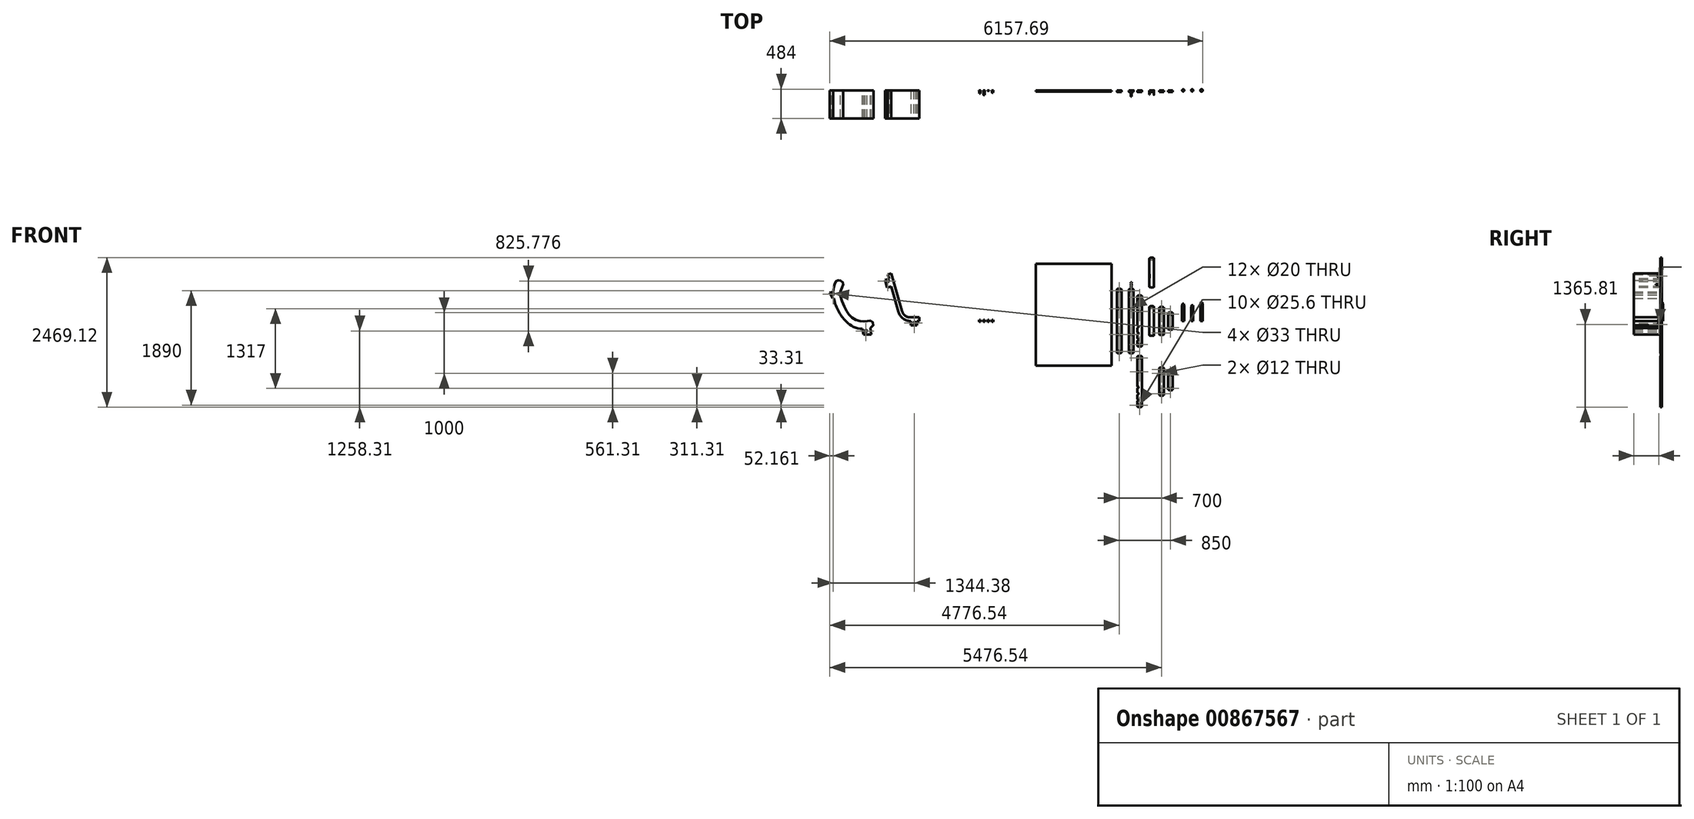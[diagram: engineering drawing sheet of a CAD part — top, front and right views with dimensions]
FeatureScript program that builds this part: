
annotation { "Feature Type Name" : "Feature", "Feature Type Description" : "" }
export const myFeature = defineFeature(function(context is Context, id is Id, definition is map)
    precondition{}
    {
        {
            var Q0;
            Q0=qCreatedBy(makeId("Front.planeOp"),FACE);
            var sketch = newSketch(context, id + "F0", { "sketchPlane" : qUnion([Q0])});
            skLineSegment(sketch, "E0", {"start": v(-38.5, 525.6) * mm, "end": v(-38.5, -525.6) * mm});
            skLineSegment(sketch, "E1", {"start": v(-38.5, -525.6) * mm, "end": v(38.5, -525.6) * mm, "construction": true});
            skLineSegment(sketch, "E2", {"start": v(38.5, -525.6) * mm, "end": v(38.5, 525.6) * mm});
            skLineSegment(sketch, "E3", {"start": v(38.5, 525.6) * mm, "end": v(-38.5, 525.6) * mm, "construction": true});
            skArc(sketch, "E4", {"start": v(38.5, 525.6) * mm, "mid": v(0, 533.3) * mm, "end": v(-38.5, 525.6) * mm});
            skArc(sketch, "E5", {"start": v(-38.5, -525.6) * mm, "mid": v(0, -533.3) * mm, "end": v(38.5, -525.6) * mm});
            skCircle(sketch, "E6", {"center": v(0, 500) * mm, "radius": 12.8 * mm});
            skCircle(sketch, "E7", {"center": v(0, -500) * mm, "radius": 12.8 * mm});
            skPoint(sketch, "E7.centerSnap0", {"position": v(0, 533.3) * mm});
            skCircle(sketch, "E8", {"center": v(0, 205) * mm, "radius": 10 * mm});
            skCircle(sketch, "E9", {"center": v(0, -225) * mm, "radius": 10 * mm});
            skSolve(sketch);
        }
        {
            var Q0;
            Q0=qSketchRegion(id+"F0",true);
            extrude(context, id + "F1", {"entities" : qUnion([Q0]), "depth" : 25 * mm, "offsetDistance" : 25 * mm});
        }
        {
            var Q0;
            Q0=qCreatedBy(makeId("Front.planeOp"),FACE);
            var sketch = newSketch(context, id + "F2", { "sketchPlane" : qUnion([Q0])});
            skCircle(sketch, "E10", {"center": v(138.5, 390) * mm, "radius": 12.8 * mm});
            skCircle(sketch, "E11", {"center": v(138.5, -390) * mm, "radius": 12.8 * mm});
            skLineSegment(sketch, "E12", {"start": v(100, 415.6) * mm, "end": v(100, -415.6) * mm});
            skLineSegment(sketch, "E13", {"start": v(177, 415.6) * mm, "end": v(177, -415.6) * mm});
            skLineSegment(sketch, "E14", {"start": v(138.5, 390) * mm, "end": v(138.5, -390) * mm, "construction": true});
            skLineSegment(sketch, "E15", {"start": v(100, -415.6) * mm, "end": v(177, -415.6) * mm, "construction": true});
            skLineSegment(sketch, "E16", {"start": v(100, 415.6) * mm, "end": v(177, 415.6) * mm, "construction": true});
            skArc(sketch, "E17", {"start": v(177, 415.6) * mm, "mid": v(138.5, 423.3) * mm, "end": v(100, 415.6) * mm});
            skArc(sketch, "E18", {"start": v(100, -415.6) * mm, "mid": v(138.5, -423.3) * mm, "end": v(177, -415.6) * mm});
            skCircle(sketch, "E19", {"center": v(138.5, 160) * mm, "radius": 10 * mm});
            skCircle(sketch, "E20", {"center": v(138.5, -96) * mm, "radius": 12.8 * mm, "construction": true});
            skSolve(sketch);
        }
        {
            var Q0;
            Q0=qSketchRegion(id+"F2",true);
            extrude(context, id + "F3", {"entities" : qUnion([Q0]), "depth" : 25 * mm, "offsetDistance" : 25 * mm});
        }
        {
            var Q0;
            Q0=qCreatedBy(makeId("Front.planeOp"),FACE);
            var sketch = newSketch(context, id + "F4", { "sketchPlane" : qUnion([Q0])});
            skLineSegment(sketch, "E21.bottom", {"start": v(300, 238.1) * mm, "end": v(377, 238.1) * mm, "construction": true});
            skLineSegment(sketch, "E21.top", {"start": v(300, -238.1) * mm, "end": v(377, -238.1) * mm, "construction": true});
            skLineSegment(sketch, "E21.left", {"start": v(300, 238.1) * mm, "end": v(300, -238.1) * mm});
            skLineSegment(sketch, "E21.right", {"start": v(377, 238.1) * mm, "end": v(377, -238.1) * mm});
            skArc(sketch, "E22", {"start": v(377, 238.1) * mm, "mid": v(338.5, 245.8) * mm, "end": v(300, 238.1) * mm});
            skArc(sketch, "E23", {"start": v(300, -238.1) * mm, "mid": v(338.5, -245.8) * mm, "end": v(377, -238.1) * mm});
            skLineSegment(sketch, "E24", {"start": v(317.98, 212.5) * mm, "end": v(377, 212.5) * mm, "construction": true});
            skLineSegment(sketch, "E25", {"start": v(309.25, -212.5) * mm, "end": v(377, -212.5) * mm, "construction": true});
            skSolve(sketch);
        }
        {
            var Q0;
            Q0=qSketchRegion(id+"F4",true);
            extrude(context, id + "F5", {"entities" : qUnion([Q0]), "depth" : 25 * mm, "offsetDistance" : 25 * mm});
        }
        {
            var Q0;
            Q0=makeQuery(id+"F5.opExtrude","SWEPT_FACE",FACE,{"disambiguationData":[OSD([sQuery(id+"F4.wireOp",EDGE,"E21.right")])]});
            var sketch = newSketch(context, id + "F6", { "sketchPlane" : qUnion([Q0])});
            skCircle(sketch, "E26", {"center": v(-12.5, 212.5) * mm, "radius": 6 * mm});
            skSolve(sketch);
        }
        {
            var Q0;
            Q0=qSketchRegion(id+"F6",true);
            var Q1;
            Q1=makeQuery(id+"F5.opExtrude","SWEPT_FACE",FACE,{"disambiguationData":[OSD([sQuery(id+"F4.wireOp",EDGE,"E21.left")])]});
            extrude(context, id + "F7", {"entities" : qUnion([Q0]), "operationType" : NewBodyOperationType.REMOVE, "endBound" : BoundingType.UP_TO_SURFACE, "oppositeDirection" : true, "depth" : 77 * mm, "endBoundEntityFace" : qUnion([Q1]), "offsetDistance" : 25 * mm});
        }
        {
            var Q0;
            Q0=makeQuery(id+"F1.opExtrude","SWEPT_EDGE",EDGE,{"disambiguationData":[OSD([sQuery(id+"F0.wireOp",EDGE,"E2"),sQuery(id+"F0.wireOp",EDGE,"E4")])]});
            var Q1;
            Q1=makeQuery(id+"F1.opExtrude","SWEPT_EDGE",EDGE,{"disambiguationData":[OSD([sQuery(id+"F0.wireOp",EDGE,"E0"),sQuery(id+"F0.wireOp",EDGE,"E4")])]});
            var Q2;
            Q2=makeQuery(id+"F1.opExtrude","SWEPT_EDGE",EDGE,{"disambiguationData":[OSD([sQuery(id+"F0.wireOp",EDGE,"E2"),sQuery(id+"F0.wireOp",EDGE,"E5")])]});
            var Q3;
            Q3=makeQuery(id+"F1.opExtrude","SWEPT_EDGE",EDGE,{"disambiguationData":[OSD([sQuery(id+"F0.wireOp",EDGE,"E0"),sQuery(id+"F0.wireOp",EDGE,"E5")])]});
            var Q4;
            Q4=makeQuery(id+"F3.opExtrude","SWEPT_EDGE",EDGE,{"disambiguationData":[OSD([sQuery(id+"F2.wireOp",EDGE,"E12"),sQuery(id+"F2.wireOp",EDGE,"E18")])]});
            var Q5;
            Q5=makeQuery(id+"F3.opExtrude","SWEPT_EDGE",EDGE,{"disambiguationData":[OSD([sQuery(id+"F2.wireOp",EDGE,"E13"),sQuery(id+"F2.wireOp",EDGE,"E18")])]});
            var Q6;
            Q6=makeQuery(id+"F3.opExtrude","SWEPT_EDGE",EDGE,{"disambiguationData":[OSD([sQuery(id+"F2.wireOp",EDGE,"E12"),sQuery(id+"F2.wireOp",EDGE,"E17")])]});
            var Q7;
            Q7=makeQuery(id+"F3.opExtrude","SWEPT_EDGE",EDGE,{"disambiguationData":[OSD([sQuery(id+"F2.wireOp",EDGE,"E13"),sQuery(id+"F2.wireOp",EDGE,"E17")])]});
            var Q8;
            Q8=makeQuery(id+"F5.opExtrude","SWEPT_EDGE",EDGE,{"disambiguationData":[OSD([sQuery(id+"F4.wireOp",EDGE,"E21.right"),sQuery(id+"F4.wireOp",EDGE,"E23")])]});
            var Q9;
            Q9=makeQuery(id+"F5.opExtrude","SWEPT_EDGE",EDGE,{"disambiguationData":[OSD([sQuery(id+"F4.wireOp",EDGE,"E21.left"),sQuery(id+"F4.wireOp",EDGE,"E23")])]});
            var Q10;
            Q10=makeQuery(id+"F5.opExtrude","SWEPT_EDGE",EDGE,{"disambiguationData":[OSD([sQuery(id+"F4.wireOp",EDGE,"E21.right"),sQuery(id+"F4.wireOp",EDGE,"E22")])]});
            var Q11;
            Q11=makeQuery(id+"F5.opExtrude","SWEPT_EDGE",EDGE,{"disambiguationData":[OSD([sQuery(id+"F4.wireOp",EDGE,"E21.left"),sQuery(id+"F4.wireOp",EDGE,"E22")])]});
            fillet(context, id + "F8", {"entities" : qUnion([Q0, Q1, Q2, Q3, Q4, Q5, Q6, Q7, Q8, Q9, Q10, Q11]), "radius" : 10 * mm, "tangentPropagation" : true, "allowEdgeOverflow" : false});
        }
        {
            var Q0;
            Q0=qCreatedBy(makeId("Front.planeOp"),FACE);
            var sketch = newSketch(context, id + "F9", { "sketchPlane" : qUnion([Q0])});
            skLineSegment(sketch, "E27.bottom", {"start": v(461.5, 225.6) * mm, "end": v(538.5, 225.6) * mm, "construction": true});
            skLineSegment(sketch, "E27.top", {"start": v(461.5, -225.6) * mm, "end": v(538.5, -225.6) * mm, "construction": true});
            skLineSegment(sketch, "E27.left", {"start": v(461.5, 225.6) * mm, "end": v(461.5, -225.6) * mm});
            skLineSegment(sketch, "E27.right", {"start": v(538.5, 225.6) * mm, "end": v(538.5, -225.6) * mm});
            skCircle(sketch, "E28", {"center": v(500, 200) * mm, "radius": 10 * mm});
            skCircle(sketch, "E29", {"center": v(500, -200) * mm, "radius": 12.8 * mm});
            skLineSegment(sketch, "E30", {"start": v(500, 200) * mm, "end": v(500, -200) * mm, "construction": true});
            skArc(sketch, "E31", {"start": v(461.5, -225.6) * mm, "mid": v(500, -233.3) * mm, "end": v(538.5, -225.6) * mm});
            skArc(sketch, "E32", {"start": v(538.5, 225.6) * mm, "mid": v(500, 233.3) * mm, "end": v(461.5, 225.6) * mm});
            skCircle(sketch, "E33", {"center": v(500, 138) * mm, "radius": 6 * mm});
            skSolve(sketch);
        }
        {
            var Q0;
            Q0=qSketchRegion(id+"F9",true);
            extrude(context, id + "F10", {"entities" : qUnion([Q0]), "depth" : 25 * mm, "offsetDistance" : 25 * mm});
        }
        {
            var Q0;
            Q0=qCreatedBy(makeId("Front.planeOp"),FACE);
            var sketch = newSketch(context, id + "F11", { "sketchPlane" : qUnion([Q0])});
            skLineSegment(sketch, "E34.bottom", {"start": v(611.5, 135.6) * mm, "end": v(688.5, 135.6) * mm, "construction": true});
            skLineSegment(sketch, "E34.top", {"start": v(611.5, -137.6) * mm, "end": v(688.5, -137.6) * mm, "construction": true});
            skLineSegment(sketch, "E34.left", {"start": v(611.5, 135.6) * mm, "end": v(611.5, -137.6) * mm});
            skLineSegment(sketch, "E34.right", {"start": v(688.5, 135.6) * mm, "end": v(688.5, -137.6) * mm});
            skCircle(sketch, "E35", {"center": v(650, 110) * mm, "radius": 10 * mm});
            skCircle(sketch, "E36", {"center": v(650, -112) * mm, "radius": 10 * mm});
            skLineSegment(sketch, "E37", {"start": v(650, 110) * mm, "end": v(650, -112) * mm, "construction": true});
            skArc(sketch, "E38", {"start": v(688.5, 135.6) * mm, "mid": v(650, 143.3) * mm, "end": v(611.5, 135.6) * mm});
            skArc(sketch, "E39", {"start": v(611.5, -137.6) * mm, "mid": v(650, -145.3) * mm, "end": v(688.5, -137.6) * mm});
            skLineSegment(sketch, "E40", {"start": v(591.68, 162.5) * mm, "end": v(739.94, 162.5) * mm, "construction": true});
            skSolve(sketch);
        }
        {
            var Q0;
            Q0=qSketchRegion(id+"F11",true);
            extrude(context, id + "F12", {"entities" : qUnion([Q0]), "depth" : 25 * mm, "offsetDistance" : 25 * mm});
        }
        {
            var Q0;
            Q0=qCreatedBy(makeId("Front.planeOp"),FACE);
            var sketch = newSketch(context, id + "F13", { "sketchPlane" : qUnion([Q0])});
            skLineSegment(sketch, "E41.bottom", {"start": v(-1573.72, 942.98) * mm, "end": v(-325.98, 942.98) * mm});
            skLineSegment(sketch, "E41.top", {"start": v(-1573.72, -735.53) * mm, "end": v(-325.98, -735.53) * mm});
            skLineSegment(sketch, "E41.left", {"start": v(-1573.72, 942.98) * mm, "end": v(-1573.72, -735.53) * mm});
            skLineSegment(sketch, "E41.right", {"start": v(-325.98, 942.98) * mm, "end": v(-325.98, -735.53) * mm});
            skSolve(sketch);
        }
        {
            var Q0;
            Q0=qSketchRegion(id+"F13",true);
            extrude(context, id + "F14", {"entities" : qUnion([Q0]), "depth" : 20 * mm, "offsetDistance" : 25 * mm});
        }
        {
            var Q0;
            Q0=qCreatedBy(makeId("Top.planeOp"),FACE);
            var sketch = newSketch(context, id + "F15", { "sketchPlane" : qUnion([Q0])});
            skCircle(sketch, "E42", {"center": v(857.86, 0) * mm, "radius": 17.5 * mm});
            skSolve(sketch);
        }
        {
            var Q0;
            Q0=qSketchRegion(id+"F15",true);
            extrude(context, id + "F16", {"entities" : qUnion([Q0]), "depth" : 257 * mm, "offsetDistance" : 25 * mm, "hasSecondDirection" : true, "secondDirectionOppositeDirection" : true, "secondDirectionDepth" : 257 * mm});
        }
        {
            var Q0;
            Q0=qCreatedBy(makeId("Top.planeOp"),FACE);
            var sketch = newSketch(context, id + "F17", { "sketchPlane" : qUnion([Q0])});
            skCircle(sketch, "E43", {"center": v(1007, 0) * mm, "radius": 17.5 * mm});
            skSolve(sketch);
        }
        {
            var Q0;
            Q0=qSketchRegion(id+"F17",true);
            extrude(context, id + "F18", {"entities" : qUnion([Q0]), "depth" : 232 * mm, "offsetDistance" : 25 * mm, "hasSecondDirection" : true, "secondDirectionOppositeDirection" : true, "secondDirectionDepth" : 232 * mm});
        }
        {
            var Q0;
            Q0=qCreatedBy(makeId("Top.planeOp"),FACE);
            var sketch = newSketch(context, id + "F19", { "sketchPlane" : qUnion([Q0])});
            skCircle(sketch, "E44", {"center": v(1161.15, 0) * mm, "radius": 20 * mm});
            skSolve(sketch);
        }
        {
            var Q0;
            Q0=qSketchRegion(id+"F19",true);
            extrude(context, id + "F20", {"entities" : qUnion([Q0]), "depth" : 282 * mm, "offsetDistance" : 25 * mm, "hasSecondDirection" : true, "secondDirectionOppositeDirection" : true, "secondDirectionDepth" : 282 * mm});
        }
        {
            var Q0;
            Q0=makeQuery(id+"F3.opExtrude","CAP_FACE",FACE,{"disambiguationData":[OSD([sQuery(id+"F2.wireOp",EDGE,"E10"),sQuery(id+"F2.wireOp",EDGE,"E11"),sQuery(id+"F2.wireOp",EDGE,"E12"),sQuery(id+"F2.wireOp",EDGE,"E13"),sQuery(id+"F2.wireOp",EDGE,"E17"),sQuery(id+"F2.wireOp",EDGE,"E18"),sQuery(id+"F2.wireOp",EDGE,"E19")])],"isStart":false});
            var sketch = newSketch(context, id + "F21", { "sketchPlane" : qUnion([Q0])});
            skCircle(sketch, "E45", {"center": v(100, -96) * mm, "radius": 20 * mm});
            skLineSegment(sketch, "E46", {"start": v(138.5, 160) * mm, "end": v(59.14, 160) * mm, "construction": true});
            skSolve(sketch);
        }
        {
            var Q0;
            Q0=qSketchRegion(id+"F21",true);
            extrude(context, id + "F22", {"entities" : qUnion([Q0]), "operationType" : NewBodyOperationType.REMOVE, "oppositeDirection" : true, "depth" : 25 * mm, "offsetDistance" : 25 * mm});
        }
        {
            var Q0;
            Q0=makeQuery(id+"F5.opExtrude","SWEPT_FACE",FACE,{"disambiguationData":[OSD([sQuery(id+"F4.wireOp",EDGE,"E21.right")])]});
            var sketch = newSketch(context, id + "F23", { "sketchPlane" : qUnion([Q0])});
            skLineSegment(sketch, "E47", {"start": v(-28, -27.5) * mm, "end": v(-28, -87.5) * mm});
            skLineSegment(sketch, "E48", {"start": v(-28, -87.5) * mm, "end": v(-59.23, -76.33) * mm});
            skLineSegment(sketch, "E49", {"start": v(-28, -27.5) * mm, "end": v(-59.23, -38.67) * mm});
            skArc(sketch, "E50", {"start": v(-59.23, -38.67) * mm, "mid": v(-72.5, -57.5) * mm, "end": v(-59.23, -76.33) * mm});
            skCircle(sketch, "E51", {"center": v(-52.5, -57.5) * mm, "radius": 10 * mm});
            skLineSegment(sketch, "E52", {"start": v(-52.5, -57.5) * mm, "end": v(29.16, -57.5) * mm, "construction": true});
            skCircle(sketch, "E53.0", {"center": v(-12.5, 212.5) * mm, "radius": 6 * mm, "construction": true});
            skSolve(sketch);
        }
        {
            var Q0;
            Q0=makeQuery(id+"F5.opExtrude","CAP_FACE",FACE,{"disambiguationData":[OSD([sQuery(id+"F4.wireOp",EDGE,"E21.left"),sQuery(id+"F4.wireOp",EDGE,"E21.right"),sQuery(id+"F4.wireOp",EDGE,"E22"),sQuery(id+"F4.wireOp",EDGE,"E23")])],"isStart":false});
            var sketch = newSketch(context, id + "F24", { "sketchPlane" : qUnion([Q0])});
            skLineSegment(sketch, "E54.bottom", {"start": v(372, -27.5) * mm, "end": v(377, -27.5) * mm});
            skLineSegment(sketch, "E54.top", {"start": v(372, -87.5) * mm, "end": v(377, -87.5) * mm});
            skLineSegment(sketch, "E54.left", {"start": v(372, -27.5) * mm, "end": v(372, -87.5) * mm});
            skLineSegment(sketch, "E54.right", {"start": v(377, -27.5) * mm, "end": v(377, -87.5) * mm});
            skSolve(sketch);
        }
        {
            var Q0;
            Q0=makeQuery(id+"F5.opExtrude","SWEPT_BODY",BODY,{"disambiguationData":[OSD([sQuery(id+"F4.wireOp",EDGE,"E21.left"),sQuery(id+"F4.wireOp",EDGE,"E21.right"),sQuery(id+"F4.wireOp",EDGE,"E22"),sQuery(id+"F4.wireOp",EDGE,"E23")])]});
            transform(context, id + "F25", {"entities" : qUnion([Q0]), "transformType" : TransformType.TRANSLATION_3D, "dx" : 0 * mm, "dy" : 0 * mm, "dz" : 800 * mm, "makeCopy" : true});
        }
        {
            var Q0;
            Q0=makeQuery(id+"F24.imprint","IMPRINT",FACE,{"disambiguationData":[TD([[makeQuery(id+"F24.imprint","IMPRINT",EDGE,{"derivedFrom":sQuery(id+"F24.wireOp",EDGE,"E54.bottom")}),-1.0]])]});
            extrude(context, id + "F26", {"entities" : qUnion([Q0]), "operationType" : NewBodyOperationType.ADD, "depth" : 3 * mm, "offsetDistance" : 25 * mm});
        }
        {
            var Q0;
            Q0=makeQuery(id+"F3.opExtrude","CAP_FACE",FACE,{"disambiguationData":[OSD([sQuery(id+"F2.wireOp",EDGE,"E10"),sQuery(id+"F2.wireOp",EDGE,"E11"),sQuery(id+"F2.wireOp",EDGE,"E12"),sQuery(id+"F2.wireOp",EDGE,"E13"),sQuery(id+"F2.wireOp",EDGE,"E17"),sQuery(id+"F2.wireOp",EDGE,"E18"),sQuery(id+"F2.wireOp",EDGE,"E19")])],"isStart":false});
            var sketch = newSketch(context, id + "F27", { "sketchPlane" : qUnion([Q0])});
            skCircle(sketch, "E55", {"center": v(100, -306) * mm, "radius": 20 * mm});
            skArc(sketch, "E56.0", {"start": v(100, -116) * mm, "mid": v(120, -96) * mm, "end": v(100, -76) * mm, "construction": true});
            skCircle(sketch, "E57", {"center": v(100, -201) * mm, "radius": 20 * mm});
            skSolve(sketch);
        }
        {
            var Q0;
            Q0=qSketchRegion(id+"F27",true);
            extrude(context, id + "F28", {"entities" : qUnion([Q0]), "operationType" : NewBodyOperationType.REMOVE, "oppositeDirection" : true, "depth" : 25 * mm, "offsetDistance" : 25 * mm});
        }
        {
            var Q0;
            Q0=qSketchRegion(id+"F23",true);
            extrude(context, id + "F29", {"entities" : qUnion([Q0]), "operationType" : NewBodyOperationType.ADD, "oppositeDirection" : true, "depth" : 5 * mm, "offsetDistance" : 25 * mm});
        }
        {
            var Q0;
            Q0=makeQuery(id+"F22.boolean.opBoolean","COPY",FACE,{"derivedFrom":makeQuery(id+"F22.opExtrude","SWEPT_FACE",FACE,{"disambiguationData":[OSD([sQuery(id+"F21.wireOp",EDGE,"E45")])]})});
            var Q1;
            Q1=makeQuery(id+"F28.boolean.opBoolean","COPY",FACE,{"derivedFrom":makeQuery(id+"F28.opExtrude","SWEPT_FACE",FACE,{"disambiguationData":[OSD([sQuery(id+"F27.wireOp",EDGE,"E57")])]})});
            var Q2;
            Q2=makeQuery(id+"F28.boolean.opBoolean","COPY",FACE,{"derivedFrom":makeQuery(id+"F28.opExtrude","SWEPT_FACE",FACE,{"disambiguationData":[OSD([sQuery(id+"F27.wireOp",EDGE,"E55")])]})});
            fillet(context, id + "F30", {"entities" : qUnion([Q0, Q1, Q2]), "radius" : 2 * mm, "tangentPropagation" : true, "allowEdgeOverflow" : false});
        }
        {
            var Q0;
            Q0=qCreatedBy(makeId("Front.planeOp"),FACE);
            var sketch = newSketch(context, id + "F31", { "sketchPlane" : qUnion([Q0])});
            skLineSegment(sketch, "E58", {"start": v(-3800, 0) * mm, "end": v(-3500, 0) * mm});
            skLineSegment(sketch, "E59", {"start": v(-3500, 0) * mm, "end": v(-3500, 60) * mm});
            skLineSegment(sketch, "E60", {"start": v(-3500, 60) * mm, "end": v(-3754.65, 60) * mm});
            skLineSegment(sketch, "E61", {"start": v(-3754.65, 60) * mm, "end": v(-3960.53, 786.02) * mm});
            skLineSegment(sketch, "E62", {"start": v(-3960.53, 786.02) * mm, "end": v(-4018.26, 769.65) * mm});
            skLineSegment(sketch, "E63", {"start": v(-4018.26, 769.65) * mm, "end": v(-3800, 0) * mm});
            skSolve(sketch);
        }
        {
            var Q0;
            Q0=qSketchRegion(id+"F31",true);
            extrude(context, id + "F32", {"entities" : qUnion([Q0]), "depth" : 464 * mm, "offsetDistance" : 25 * mm});
        }
        {
            var Q0;
            Q0=makeQuery(id+"F1.opExtrude","SWEPT_BODY",BODY,{"disambiguationData":[OSD([sQuery(id+"F0.wireOp",EDGE,"E0"),sQuery(id+"F0.wireOp",EDGE,"E2"),sQuery(id+"F0.wireOp",EDGE,"E4"),sQuery(id+"F0.wireOp",EDGE,"E5"),sQuery(id+"F0.wireOp",EDGE,"E6"),sQuery(id+"F0.wireOp",EDGE,"E7"),sQuery(id+"F0.wireOp",EDGE,"E8"),sQuery(id+"F0.wireOp",EDGE,"E9")])]});
            transform(context, id + "F33", {"entities" : qUnion([Q0]), "transformType" : TransformType.TRANSLATION_3D, "dx" : -200 * mm, "dy" : 0 * mm, "dz" : 0 * mm, "makeCopy" : true});
        }
        {
            var Q0;
            Q0=makeQuery(id+"F3.opExtrude","SWEPT_BODY",BODY,{"disambiguationData":[OSD([sQuery(id+"F2.wireOp",EDGE,"E10"),sQuery(id+"F2.wireOp",EDGE,"E11"),sQuery(id+"F2.wireOp",EDGE,"E12"),sQuery(id+"F2.wireOp",EDGE,"E13"),sQuery(id+"F2.wireOp",EDGE,"E17"),sQuery(id+"F2.wireOp",EDGE,"E18"),sQuery(id+"F2.wireOp",EDGE,"E19")])]});
            transform(context, id + "F34", {"entities" : qUnion([Q0]), "transformType" : TransformType.TRANSLATION_3D, "dx" : 0 * mm, "dy" : 0 * mm, "dz" : -1000 * mm, "makeCopy" : true});
        }
        {
            var Q0;
            Q0=makeQuery(id+"F10.opExtrude","SWEPT_BODY",BODY,{"disambiguationData":[OSD([sQuery(id+"F9.wireOp",EDGE,"E27.left"),sQuery(id+"F9.wireOp",EDGE,"E27.right"),sQuery(id+"F9.wireOp",EDGE,"E28"),sQuery(id+"F9.wireOp",EDGE,"E29"),sQuery(id+"F9.wireOp",EDGE,"E31"),sQuery(id+"F9.wireOp",EDGE,"E32"),sQuery(id+"F9.wireOp",EDGE,"E33")])]});
            transform(context, id + "F35", {"entities" : qUnion([Q0]), "transformType" : TransformType.TRANSLATION_3D, "dx" : 0 * mm, "dy" : 0 * mm, "dz" : -1000 * mm, "makeCopy" : true});
        }
        {
            var Q0;
            Q0=makeQuery(id+"F12.opExtrude","SWEPT_BODY",BODY,{"disambiguationData":[OSD([sQuery(id+"F11.wireOp",EDGE,"E34.left"),sQuery(id+"F11.wireOp",EDGE,"E34.right"),sQuery(id+"F11.wireOp",EDGE,"E35"),sQuery(id+"F11.wireOp",EDGE,"E36"),sQuery(id+"F11.wireOp",EDGE,"E38"),sQuery(id+"F11.wireOp",EDGE,"E39")])]});
            transform(context, id + "F36", {"entities" : qUnion([Q0]), "transformType" : TransformType.TRANSLATION_3D, "dx" : 0 * mm, "dy" : 0 * mm, "dz" : -1000 * mm, "makeCopy" : true});
        }
        {
            var Q0;
            Q0=makeQuery(id+"F32.opExtrude","SWEPT_EDGE",EDGE,{"disambiguationData":[OSD([sQuery(id+"F31.wireOp",EDGE,"E58"),sQuery(id+"F31.wireOp",EDGE,"E63")])]});
            fillet(context, id + "F37", {"entities" : qUnion([Q0]), "radius" : 200 * mm, "tangentPropagation" : true, "allowEdgeOverflow" : false});
        }
        {
            var Q0;
            Q0=makeQuery(id+"F32.opExtrude","SWEPT_EDGE",EDGE,{"disambiguationData":[OSD([sQuery(id+"F31.wireOp",EDGE,"E60"),sQuery(id+"F31.wireOp",EDGE,"E61")])]});
            fillet(context, id + "F38", {"entities" : qUnion([Q0]), "radius" : 140 * mm, "tangentPropagation" : true, "allowEdgeOverflow" : false});
        }
        {
            var Q0;
            Q0=makeQuery(id+"F32.opExtrude","CAP_FACE",FACE,{"disambiguationData":[OSD([sQuery(id+"F31.wireOp",EDGE,"E58"),sQuery(id+"F31.wireOp",EDGE,"E59"),sQuery(id+"F31.wireOp",EDGE,"E60"),sQuery(id+"F31.wireOp",EDGE,"E61"),sQuery(id+"F31.wireOp",EDGE,"E62"),sQuery(id+"F31.wireOp",EDGE,"E63")])],"isStart":false});
            var sketch = newSketch(context, id + "F39", { "sketchPlane" : qUnion([Q0])});
            skPoint(sketch, "E64", {"position": v(-4018.56, 660.78) * mm});
            skPoint(sketch, "E65", {"position": v(-3580, -30) * mm});
            skLineSegment(sketch, "E66", {"start": v(-4018.56, 660.78) * mm, "end": v(-3931.98, 685.33) * mm, "construction": true});
            skLineSegment(sketch, "E67", {"start": v(-3580, -30) * mm, "end": v(-3580, 60) * mm, "construction": true});
            skCircle(sketch, "E68", {"center": v(-4018.56, 660.78) * mm, "radius": 16.5 * mm});
            skCircle(sketch, "E69", {"center": v(-3580, -30) * mm, "radius": 16.5 * mm});
            skLineSegment(sketch, "E70", {"start": v(-3997.89, 697.82) * mm, "end": v(-4065.23, 678.73) * mm});
            skLineSegment(sketch, "E71", {"start": v(-4065.23, 678.73) * mm, "end": v(-4029.77, 553.66) * mm});
            skLineSegment(sketch, "E72", {"start": v(-4029.77, 553.66) * mm, "end": v(-3962.42, 572.75) * mm});
            skLineSegment(sketch, "E73.bottom", {"start": v(-3540, 0) * mm, "end": v(-3640, 0) * mm});
            skLineSegment(sketch, "E73.top", {"start": v(-3540, -70) * mm, "end": v(-3640, -70) * mm});
            skLineSegment(sketch, "E73.left", {"start": v(-3540, 0) * mm, "end": v(-3540, -70) * mm});
            skLineSegment(sketch, "E73.right", {"start": v(-3640, 0) * mm, "end": v(-3640, -70) * mm});
            skSolve(sketch);
        }
        {
            var Q0;
            Q0=makeQuery(id+"F39.imprint","IMPRINT",FACE,{"disambiguationData":[TD([[makeQuery(id+"F39.imprint","IMPRINT",EDGE,{"derivedFrom":sQuery(id+"F39.wireOp",EDGE,"E69")}),-1.0]])]});
            var Q1;
            Q1=makeQuery(id+"F39.imprint","IMPRINT",FACE,{"disambiguationData":[TD([[makeQuery(id+"F39.imprint","IMPRINT",EDGE,{"derivedFrom":sQuery(id+"F39.wireOp",EDGE,"E68")}),-1.0]])]});
            var Q2;
            Q2=makeQuery(id+"F32.opExtrude","CAP_FACE",FACE,{"disambiguationData":[OSD([sQuery(id+"F31.wireOp",EDGE,"E58"),sQuery(id+"F31.wireOp",EDGE,"E59"),sQuery(id+"F31.wireOp",EDGE,"E60"),sQuery(id+"F31.wireOp",EDGE,"E61"),sQuery(id+"F31.wireOp",EDGE,"E62"),sQuery(id+"F31.wireOp",EDGE,"E63")])],"isStart":true});
            extrude(context, id + "F40", {"entities" : qUnion([Q0, Q1]), "operationType" : NewBodyOperationType.ADD, "endBound" : BoundingType.UP_TO_SURFACE, "oppositeDirection" : true, "depth" : 25 * mm, "endBoundEntityFace" : qUnion([Q2]), "offsetDistance" : 25 * mm});
        }
        {
            var Q0;
            Q0=makeQuery(id+"F16.opExtrude","CAP_FACE",FACE,{"disambiguationData":[OSD([sQuery(id+"F15.wireOp",EDGE,"E42")])],"isStart":false});
            var sketch = newSketch(context, id + "F41", { "sketchPlane" : qUnion([Q0])});
            skCircle(sketch, "E74", {"center": v(857.86, 0) * mm, "radius": 12.8 * mm});
            skSolve(sketch);
        }
        {
            var Q0;
            Q0=qSketchRegion(id+"F41",true);
            extrude(context, id + "F42", {"entities" : qUnion([Q0]), "operationType" : NewBodyOperationType.ADD, "depth" : 25 * mm, "offsetDistance" : 25 * mm});
        }
        {
            var Q0;
            Q0=makeQuery(id+"F16.opExtrude","CAP_FACE",FACE,{"disambiguationData":[OSD([sQuery(id+"F15.wireOp",EDGE,"E42")])],"isStart":true});
            var sketch = newSketch(context, id + "F43", { "sketchPlane" : qUnion([Q0])});
            skCircle(sketch, "E75", {"center": v(857.86, 0) * mm, "radius": 12.8 * mm});
            skSolve(sketch);
        }
        {
            var Q0;
            Q0=qSketchRegion(id+"F43",true);
            extrude(context, id + "F44", {"entities" : qUnion([Q0]), "operationType" : NewBodyOperationType.ADD, "depth" : 25 * mm, "offsetDistance" : 25 * mm});
        }
        {
            var Q0;
            Q0=makeQuery(id+"F18.opExtrude","CAP_FACE",FACE,{"disambiguationData":[OSD([sQuery(id+"F17.wireOp",EDGE,"E43")])],"isStart":true});
            var sketch = newSketch(context, id + "F45", { "sketchPlane" : qUnion([Q0])});
            skCircle(sketch, "E76", {"center": v(1007, 0) * mm, "radius": 12.8 * mm});
            skSolve(sketch);
        }
        {
            var Q0;
            Q0=qSketchRegion(id+"F45",true);
            extrude(context, id + "F46", {"entities" : qUnion([Q0]), "operationType" : NewBodyOperationType.ADD, "depth" : 25 * mm, "offsetDistance" : 25 * mm});
        }
        {
            var Q0;
            Q0=makeQuery(id+"F18.opExtrude","CAP_FACE",FACE,{"disambiguationData":[OSD([sQuery(id+"F17.wireOp",EDGE,"E43")])],"isStart":false});
            var sketch = newSketch(context, id + "F47", { "sketchPlane" : qUnion([Q0])});
            skCircle(sketch, "E77", {"center": v(1007, 0) * mm, "radius": 12.8 * mm});
            skSolve(sketch);
        }
        {
            var Q0;
            Q0=qSketchRegion(id+"F47",true);
            extrude(context, id + "F48", {"entities" : qUnion([Q0]), "operationType" : NewBodyOperationType.ADD, "depth" : 25 * mm, "offsetDistance" : 25 * mm});
        }
        {
            var Q0;
            Q0=makeQuery(id+"F20.opExtrude","CAP_FACE",FACE,{"disambiguationData":[OSD([sQuery(id+"F19.wireOp",EDGE,"E44")])],"isStart":true});
            var sketch = newSketch(context, id + "F49", { "sketchPlane" : qUnion([Q0])});
            skCircle(sketch, "E78", {"center": v(1161.15, 0) * mm, "radius": 12.8 * mm});
            skSolve(sketch);
        }
        {
            var Q0;
            Q0=qSketchRegion(id+"F49",true);
            extrude(context, id + "F50", {"entities" : qUnion([Q0]), "operationType" : NewBodyOperationType.ADD, "depth" : 25 * mm, "offsetDistance" : 25 * mm});
        }
        {
            var Q0;
            Q0=makeQuery(id+"F20.opExtrude","CAP_FACE",FACE,{"disambiguationData":[OSD([sQuery(id+"F19.wireOp",EDGE,"E44")])],"isStart":false});
            var sketch = newSketch(context, id + "F51", { "sketchPlane" : qUnion([Q0])});
            skCircle(sketch, "E79", {"center": v(1161.15, 0) * mm, "radius": 12.8 * mm});
            skSolve(sketch);
        }
        {
            var Q0;
            Q0=qSketchRegion(id+"F51",true);
            extrude(context, id + "F52", {"entities" : qUnion([Q0]), "operationType" : NewBodyOperationType.ADD, "depth" : 25 * mm, "offsetDistance" : 25 * mm});
        }
        {
            var Q0;
            Q0=qCreatedBy(makeId("Front.planeOp"),FACE);
            var sketch = newSketch(context, id + "F53", { "sketchPlane" : qUnion([Q0])});
            skCircle(sketch, "E80", {"center": v(-2500, 0) * mm, "radius": 15 * mm, "construction": true});
            skLineSegment(sketch, "E81.0", {"start": v(-2508.66, 15) * mm, "end": v(-2491.34, 15) * mm});
            skLineSegment(sketch, "E81.1", {"start": v(-2491.34, 15) * mm, "end": v(-2482.68, 0) * mm});
            skLineSegment(sketch, "E81.2", {"start": v(-2482.68, 0) * mm, "end": v(-2491.34, -15) * mm});
            skLineSegment(sketch, "E81.3", {"start": v(-2491.34, -15) * mm, "end": v(-2508.66, -15) * mm});
            skLineSegment(sketch, "E81.4", {"start": v(-2508.66, -15) * mm, "end": v(-2517.32, 0) * mm});
            skLineSegment(sketch, "E81.5", {"start": v(-2517.32, 0) * mm, "end": v(-2508.66, 15) * mm});
            skPoint(sketch, "E81.0.midPoint", {"position": v(-2500, 15) * mm});
            skCircle(sketch, "E82", {"center": v(-2500, 0) * mm, "radius": 21 * mm, "construction": true});
            skCircle(sketch, "E83.cCircle", {"center": v(-2430, 0) * mm, "radius": 15 * mm, "construction": true});
            skLineSegment(sketch, "E83.0", {"start": v(-2438.66, 15) * mm, "end": v(-2421.34, 15) * mm});
            skLineSegment(sketch, "E83.1", {"start": v(-2421.34, 15) * mm, "end": v(-2412.68, 0) * mm});
            skLineSegment(sketch, "E83.2", {"start": v(-2412.68, 0) * mm, "end": v(-2421.34, -15) * mm});
            skLineSegment(sketch, "E83.3", {"start": v(-2421.34, -15) * mm, "end": v(-2438.66, -15) * mm});
            skLineSegment(sketch, "E83.4", {"start": v(-2438.66, -15) * mm, "end": v(-2447.32, 0) * mm});
            skLineSegment(sketch, "E83.5", {"start": v(-2447.32, 0) * mm, "end": v(-2438.66, 15) * mm});
            skPoint(sketch, "E83.0.midPoint", {"position": v(-2430, 15) * mm});
            skCircle(sketch, "E84.cCircle", {"center": v(-2360, 0) * mm, "radius": 15 * mm, "construction": true});
            skLineSegment(sketch, "E84.0", {"start": v(-2368.66, 15) * mm, "end": v(-2351.34, 15) * mm});
            skLineSegment(sketch, "E84.1", {"start": v(-2351.34, 15) * mm, "end": v(-2342.68, 0) * mm});
            skLineSegment(sketch, "E84.2", {"start": v(-2342.68, 0) * mm, "end": v(-2351.34, -15) * mm});
            skLineSegment(sketch, "E84.3", {"start": v(-2351.34, -15) * mm, "end": v(-2368.66, -15) * mm});
            skLineSegment(sketch, "E84.4", {"start": v(-2368.66, -15) * mm, "end": v(-2377.32, 0) * mm});
            skLineSegment(sketch, "E84.5", {"start": v(-2377.32, 0) * mm, "end": v(-2368.66, 15) * mm});
            skPoint(sketch, "E84.0.midPoint", {"position": v(-2360, 15) * mm});
            skCircle(sketch, "E85", {"center": v(-2360, 0) * mm, "radius": 10 * mm});
            skCircle(sketch, "E86.cCircle", {"center": v(-2290, 0) * mm, "radius": 15 * mm, "construction": true});
            skLineSegment(sketch, "E86.0", {"start": v(-2298.66, 15) * mm, "end": v(-2281.34, 15) * mm});
            skLineSegment(sketch, "E86.1", {"start": v(-2281.34, 15) * mm, "end": v(-2272.68, 0) * mm});
            skLineSegment(sketch, "E86.2", {"start": v(-2272.68, 0) * mm, "end": v(-2281.34, -15) * mm});
            skLineSegment(sketch, "E86.3", {"start": v(-2281.34, -15) * mm, "end": v(-2298.66, -15) * mm});
            skLineSegment(sketch, "E86.4", {"start": v(-2298.66, -15) * mm, "end": v(-2307.32, 0) * mm});
            skLineSegment(sketch, "E86.5", {"start": v(-2307.32, 0) * mm, "end": v(-2298.66, 15) * mm});
            skPoint(sketch, "E86.0.midPoint", {"position": v(-2290, 15) * mm});
            skSolve(sketch);
        }
        {
            var Q0;
            Q0=qSketchRegion(id+"F53",true);
            extrude(context, id + "F54", {"entities" : qUnion([Q0]), "depth" : 8 * mm, "offsetDistance" : 25 * mm});
        }
        {
            var Q0;
            Q0=makeQuery(id+"F54.opExtrude","CAP_FACE",FACE,{"disambiguationData":[OSD([sQuery(id+"F53.wireOp",EDGE,"E81.0"),sQuery(id+"F53.wireOp",EDGE,"E81.1"),sQuery(id+"F53.wireOp",EDGE,"E81.2"),sQuery(id+"F53.wireOp",EDGE,"E81.3"),sQuery(id+"F53.wireOp",EDGE,"E81.4"),sQuery(id+"F53.wireOp",EDGE,"E81.5")])],"isStart":false});
            var sketch = newSketch(context, id + "F55", { "sketchPlane" : qUnion([Q0])});
            skCircle(sketch, "E87", {"center": v(-2500, 0) * mm, "radius": 10 * mm});
            skPoint(sketch, "E87.centerSnap0", {"position": v(-2500, 15) * mm});
            skSolve(sketch);
        }
        {
            var Q0;
            Q0=qSketchRegion(id+"F55",true);
            extrude(context, id + "F56", {"entities" : qUnion([Q0]), "operationType" : NewBodyOperationType.ADD, "depth" : 42 * mm, "offsetDistance" : 25 * mm});
        }
        {
            var Q0;
            Q0=makeQuery(id+"F54.opExtrude","CAP_FACE",FACE,{"disambiguationData":[OSD([sQuery(id+"F53.wireOp",EDGE,"E83.0"),sQuery(id+"F53.wireOp",EDGE,"E83.1"),sQuery(id+"F53.wireOp",EDGE,"E83.2"),sQuery(id+"F53.wireOp",EDGE,"E83.3"),sQuery(id+"F53.wireOp",EDGE,"E83.4"),sQuery(id+"F53.wireOp",EDGE,"E83.5")])],"isStart":false});
            var sketch = newSketch(context, id + "F57", { "sketchPlane" : qUnion([Q0])});
            skCircle(sketch, "E88", {"center": v(-2430, 0) * mm, "radius": 10 * mm});
            skSolve(sketch);
        }
        {
            var Q0;
            Q0=qSketchRegion(id+"F57",true);
            extrude(context, id + "F58", {"entities" : qUnion([Q0]), "operationType" : NewBodyOperationType.ADD, "depth" : 67 * mm, "offsetDistance" : 25 * mm});
        }
        {
            var Q0;
            Q0=makeQuery(id+"F54.opExtrude","CAP_FACE",FACE,{"disambiguationData":[OSD([sQuery(id+"F53.wireOp",EDGE,"E86.0"),sQuery(id+"F53.wireOp",EDGE,"E86.1"),sQuery(id+"F53.wireOp",EDGE,"E86.2"),sQuery(id+"F53.wireOp",EDGE,"E86.3"),sQuery(id+"F53.wireOp",EDGE,"E86.4"),sQuery(id+"F53.wireOp",EDGE,"E86.5")])],"isStart":false});
            var sketch = newSketch(context, id + "F59", { "sketchPlane" : qUnion([Q0])});
            skCircle(sketch, "E89", {"center": v(-2290, 0) * mm, "radius": 10 * mm});
            skSolve(sketch);
        }
        {
            var Q0;
            Q0=qSketchRegion(id+"F59",true);
            extrude(context, id + "F60", {"entities" : qUnion([Q0]), "operationType" : NewBodyOperationType.ADD, "depth" : 30 * mm, "offsetDistance" : 25 * mm});
        }
        {
            var Q0;
            Q0=makeQuery(id+"F10.opExtrude","CAP_FACE",FACE,{"disambiguationData":[OSD([sQuery(id+"F9.wireOp",EDGE,"E27.left"),sQuery(id+"F9.wireOp",EDGE,"E27.right"),sQuery(id+"F9.wireOp",EDGE,"E28"),sQuery(id+"F9.wireOp",EDGE,"E29"),sQuery(id+"F9.wireOp",EDGE,"E31"),sQuery(id+"F9.wireOp",EDGE,"E32"),sQuery(id+"F9.wireOp",EDGE,"E33")])],"isStart":false});
            var sketch = newSketch(context, id + "F61", { "sketchPlane" : qUnion([Q0])});
            skCircle(sketch, "E90", {"center": v(500, 138) * mm, "radius": 10 * mm});
            skSolve(sketch);
        }
        {
            var Q0;
            Q0=qSketchRegion(id+"F61",true);
            extrude(context, id + "F62", {"entities" : qUnion([Q0]), "operationType" : NewBodyOperationType.REMOVE, "depth" : 8 * mm, "offsetDistance" : 25 * mm});
        }
        {
            var Q0;
            Q0=makeQuery(id+"F25.opPattern","COPY",FACE,{"derivedFrom":makeQuery(id+"F5.opExtrude","SWEPT_FACE",FACE,{"disambiguationData":[OSD([sQuery(id+"F4.wireOp",EDGE,"E21.right")])]}),"instanceName":"1"});
            var sketch = newSketch(context, id + "F63", { "sketchPlane" : qUnion([Q0])});
            skCircle(sketch, "E91", {"center": v(-12.5, 1012.5) * mm, "radius": 10 * mm});
            skSolve(sketch);
        }
        {
            var Q0;
            Q0=qCreatedBy(makeId("Front.planeOp"),FACE);
            var sketch = newSketch(context, id + "F64", { "sketchPlane" : qUnion([Q0])});
            skCircle(sketch, "E92.cCircle", {"center": v(0, 600) * mm, "radius": 8 * mm, "construction": true});
            skLineSegment(sketch, "E92.0", {"start": v(-4.62, 608) * mm, "end": v(4.62, 608) * mm});
            skLineSegment(sketch, "E92.1", {"start": v(4.62, 608) * mm, "end": v(9.24, 600) * mm});
            skLineSegment(sketch, "E92.2", {"start": v(9.24, 600) * mm, "end": v(4.62, 592) * mm});
            skLineSegment(sketch, "E92.3", {"start": v(4.62, 592) * mm, "end": v(-4.62, 592) * mm});
            skLineSegment(sketch, "E92.4", {"start": v(-4.62, 592) * mm, "end": v(-9.24, 600) * mm});
            skLineSegment(sketch, "E92.5", {"start": v(-9.24, 600) * mm, "end": v(-4.62, 608) * mm});
            skPoint(sketch, "E92.0.midPoint", {"position": v(0, 608) * mm});
            skCircle(sketch, "E93", {"center": v(0, 600) * mm, "radius": 10 * mm, "construction": true});
            skCircle(sketch, "E94.cCircle", {"center": v(0, 630) * mm, "radius": 8 * mm, "construction": true});
            skLineSegment(sketch, "E94.0", {"start": v(-4.62, 638) * mm, "end": v(4.62, 638) * mm});
            skLineSegment(sketch, "E94.1", {"start": v(4.62, 638) * mm, "end": v(9.24, 630) * mm});
            skLineSegment(sketch, "E94.2", {"start": v(9.24, 630) * mm, "end": v(4.62, 622) * mm});
            skLineSegment(sketch, "E94.3", {"start": v(4.62, 622) * mm, "end": v(-4.62, 622) * mm});
            skLineSegment(sketch, "E94.4", {"start": v(-4.62, 622) * mm, "end": v(-9.24, 630) * mm});
            skLineSegment(sketch, "E94.5", {"start": v(-9.24, 630) * mm, "end": v(-4.62, 638) * mm});
            skPoint(sketch, "E94.0.midPoint", {"position": v(0, 638) * mm});
            skCircle(sketch, "E95", {"center": v(0, 630) * mm, "radius": 6 * mm});
            skSolve(sketch);
        }
        {
            var Q0;
            Q0=makeQuery(id+"F64.imprint","IMPRINT",FACE,{"disambiguationData":[TD([[makeQuery(id+"F64.imprint","IMPRINT",EDGE,{"derivedFrom":sQuery(id+"F64.wireOp",EDGE,"E92.0")}),-1.0]])]});
            var Q1;
            Q1=makeQuery(id+"F64.imprint","IMPRINT",FACE,{"disambiguationData":[TD([[makeQuery(id+"F64.imprint","IMPRINT",EDGE,{"derivedFrom":sQuery(id+"F64.wireOp",EDGE,"E94.0")}),-1.0]])]});
            var Q2;
            Q2=sQuery(id+"F64.wireOp",EDGE,"E93");
            extrude(context, id + "F65", {"entities" : qUnion([Q0, Q1]), "surfaceEntities" : qUnion([Q2]), "depth" : 5 * mm, "offsetDistance" : 25 * mm});
        }
        {
            var Q0;
            Q0=makeQuery(id+"F65.opExtrude","CAP_FACE",FACE,{"disambiguationData":[OSD([sQuery(id+"F64.wireOp",EDGE,"E92.0"),sQuery(id+"F64.wireOp",EDGE,"E92.1"),sQuery(id+"F64.wireOp",EDGE,"E92.2"),sQuery(id+"F64.wireOp",EDGE,"E92.3"),sQuery(id+"F64.wireOp",EDGE,"E92.4"),sQuery(id+"F64.wireOp",EDGE,"E92.5")])],"isStart":false});
            var sketch = newSketch(context, id + "F66", { "sketchPlane" : qUnion([Q0])});
            skCircle(sketch, "E96", {"center": v(0, 600) * mm, "radius": 6 * mm});
            skSolve(sketch);
        }
        {
            var Q0;
            Q0=qSketchRegion(id+"F66",true);
            extrude(context, id + "F67", {"entities" : qUnion([Q0]), "operationType" : NewBodyOperationType.ADD, "depth" : 97 * mm, "offsetDistance" : 25 * mm});
        }
        {
            var Q0;
            Q0=qCreatedBy(makeId("Front.planeOp"),FACE);
            var sketch = newSketch(context, id + "F68", { "sketchPlane" : qUnion([Q0])});
            skCircle(sketch, "E97.cCircle", {"center": v(0, 570) * mm, "radius": 7 * mm, "construction": true});
            skLineSegment(sketch, "E97.0", {"start": v(-4.04, 577) * mm, "end": v(4.04, 577) * mm});
            skLineSegment(sketch, "E97.1", {"start": v(4.04, 577) * mm, "end": v(8.08, 570) * mm});
            skLineSegment(sketch, "E97.2", {"start": v(8.08, 570) * mm, "end": v(4.04, 563) * mm});
            skLineSegment(sketch, "E97.3", {"start": v(4.04, 563) * mm, "end": v(-4.04, 563) * mm});
            skLineSegment(sketch, "E97.4", {"start": v(-4.04, 563) * mm, "end": v(-8.08, 570) * mm});
            skLineSegment(sketch, "E97.5", {"start": v(-8.08, 570) * mm, "end": v(-4.04, 577) * mm});
            skPoint(sketch, "E97.0.midPoint", {"position": v(0, 577) * mm});
            skSolve(sketch);
        }
        {
            var Q0;
            Q0=qSketchRegion(id+"F68",true);
            extrude(context, id + "F69", {"entities" : qUnion([Q0]), "depth" : 3 * mm, "offsetDistance" : 25 * mm});
        }
        {
            var Q0;
            Q0=makeQuery(id+"F69.opExtrude","CAP_FACE",FACE,{"disambiguationData":[OSD([sQuery(id+"F68.wireOp",EDGE,"E97.0"),sQuery(id+"F68.wireOp",EDGE,"E97.1"),sQuery(id+"F68.wireOp",EDGE,"E97.2"),sQuery(id+"F68.wireOp",EDGE,"E97.3"),sQuery(id+"F68.wireOp",EDGE,"E97.4"),sQuery(id+"F68.wireOp",EDGE,"E97.5")])],"isStart":false});
            var sketch = newSketch(context, id + "F70", { "sketchPlane" : qUnion([Q0])});
            skCircle(sketch, "E98", {"center": v(0, 570) * mm, "radius": 4 * mm});
            skSolve(sketch);
        }
        {
            var Q0;
            Q0=qSketchRegion(id+"F70",true);
            extrude(context, id + "F71", {"entities" : qUnion([Q0]), "operationType" : NewBodyOperationType.ADD, "depth" : 13 * mm, "offsetDistance" : 25 * mm});
        }
        {
            var Q0;
            Q0=qCreatedBy(makeId("Front.planeOp"),FACE);
            var sketch = newSketch(context, id + "F72", { "sketchPlane" : qUnion([Q0])});
            skCircle(sketch, "E99", {"center": v(-4924.38, 445.87) * mm, "radius": 16.5 * mm});
            skCircle(sketch, "E100", {"center": v(-4380, -165) * mm, "radius": 16.5 * mm});
            skCircle(sketch, "E101.0", {"center": v(-3580, -30) * mm, "radius": 16.5 * mm, "construction": true});
            skCircle(sketch, "E102.0", {"center": v(-4018.56, 660.78) * mm, "radius": 16.5 * mm, "construction": true});
            skFitSpline(sketch, "E103", {"points": [v(-4285.55, 0) * mm, v(-4263.83, -82.96) * mm, v(-4527.36, -117.42) * mm, v(-4751.42, 41.89) * mm, v(-4862.59, 223.1) * mm, v(-4920.48, 440.9) * mm, v(-4897.1, 605.72) * mm, v(-4861.84, 667.96) * mm, v(-4817.48, 672.43) * mm, v(-4768.38, 645.04) * mm, v(-4760.24, 587.33) * mm, v(-4803.14, 468.85) * mm, v(-4733.68, 225.77) * mm, v(-4627.46, 70.51) * mm, v(-4480.38, 0) * mm, v(-4357.62, 0) * mm, v(-4285.55, 0) * mm]});
            skLineSegment(sketch, "E104", {"start": v(-4920.34, 482.88) * mm, "end": v(-4976.54, 468.15) * mm});
            skLineSegment(sketch, "E105", {"start": v(-4976.54, 468.15) * mm, "end": v(-4929.96, 375.69) * mm});
            skLineSegment(sketch, "E106", {"start": v(-4929.96, 375.69) * mm, "end": v(-4912.28, 375.69) * mm});
            skLineSegment(sketch, "E107", {"start": v(-4439.67, -130.69) * mm, "end": v(-4418.5, -221.82) * mm});
            skLineSegment(sketch, "E108", {"start": v(-4418.5, -221.82) * mm, "end": v(-4294.26, -221.82) * mm});
            skLineSegment(sketch, "E109", {"start": v(-4294.26, -221.82) * mm, "end": v(-4308.25, -114.89) * mm});
            skSolve(sketch);
        }
        {
            var Q0;
            Q0=qSketchRegion(id+"F72",true);
            var Q1;
            {var subQ0=sQuery(id+"F31.wireOp",EDGE,"E63");Q1=makeQuery(id+"F40.boolean.opBoolean","MERGE",FACE,{"derivedFrom":[makeQuery(id+"F32.opExtrude","CAP_FACE",FACE,{"disambiguationData":[OSD([sQuery(id+"F31.wireOp",EDGE,"E58"),sQuery(id+"F31.wireOp",EDGE,"E59"),sQuery(id+"F31.wireOp",EDGE,"E60"),sQuery(id+"F31.wireOp",EDGE,"E61"),sQuery(id+"F31.wireOp",EDGE,"E62"),subQ0])],"isStart":false}),makeQuery(id+"F40.opExtrude","CAP_FACE",FACE,{"disambiguationData":[OSD([subQ0,sQuery(id+"F39.wireOp",EDGE,"E68"),sQuery(id+"F39.wireOp",EDGE,"E70"),sQuery(id+"F39.wireOp",EDGE,"E71"),sQuery(id+"F39.wireOp",EDGE,"E72")])],"isStart":true}),makeQuery(id+"F40.opExtrude","CAP_FACE",FACE,{"disambiguationData":[OSD([sQuery(id+"F39.wireOp",EDGE,"E69"),sQuery(id+"F39.wireOp",EDGE,"E73.bottom"),sQuery(id+"F39.wireOp",EDGE,"E73.top"),sQuery(id+"F39.wireOp",EDGE,"E73.left"),sQuery(id+"F39.wireOp",EDGE,"E73.right")])],"isStart":true})]});}
            extrude(context, id + "F73", {"entities" : qUnion([Q0]), "endBound" : BoundingType.UP_TO_SURFACE, "depth" : 25 * mm, "endBoundEntityFace" : qUnion([Q1]), "offsetDistance" : 25 * mm});
        }
        {
            var Q0;
            Q0=makeQuery(id+"F25.opPattern","COPY",FACE,{"derivedFrom":makeQuery(id+"F5.opExtrude","SWEPT_FACE",FACE,{"disambiguationData":[OSD([sQuery(id+"F4.wireOp",EDGE,"E21.left")])]}),"instanceName":"1"});
            var sketch = newSketch(context, id + "F74", { "sketchPlane" : qUnion([Q0])});
            skLineSegment(sketch, "E110", {"start": v(28, 772.5) * mm, "end": v(59.23, 761.33) * mm});
            skLineSegment(sketch, "E111", {"start": v(28, 712.5) * mm, "end": v(59.23, 723.67) * mm});
            skArc(sketch, "E112", {"start": v(59.23, 723.67) * mm, "mid": v(72.5, 742.5) * mm, "end": v(59.23, 761.33) * mm});
            skLineSegment(sketch, "E113", {"start": v(28, 772.5) * mm, "end": v(25, 772.5) * mm});
            skLineSegment(sketch, "E114", {"start": v(28, 712.5) * mm, "end": v(25, 712.5) * mm});
            skLineSegment(sketch, "E115", {"start": v(25, 712.5) * mm, "end": v(25, 772.5) * mm});
            skCircle(sketch, "E116", {"center": v(52.5, 742.5) * mm, "radius": 10 * mm});
            skSolve(sketch);
        }
        {
            var Q0;
            Q0=qSketchRegion(id+"F74",true);
            extrude(context, id + "F75", {"entities" : qUnion([Q0]), "operationType" : NewBodyOperationType.ADD, "oppositeDirection" : true, "depth" : 5 * mm, "offsetDistance" : 25 * mm});
        }
        {
            var Q0;
            Q0=makeQuery(id+"F50.opExtrude","CAP_FACE",FACE,{"disambiguationData":[OSD([sQuery(id+"F49.wireOp",EDGE,"E78")])],"isStart":false});
            var sketch = newSketch(context, id + "F76", { "sketchPlane" : qUnion([Q0])});
            skLineSegment(sketch, "E117.bottom", {"start": v(806.43, 65.4) * mm, "end": v(1258.43, 65.4) * mm});
            skLineSegment(sketch, "E117.top", {"start": v(806.43, -80.21) * mm, "end": v(1258.43, -80.21) * mm});
            skLineSegment(sketch, "E117.left", {"start": v(806.43, 65.4) * mm, "end": v(806.43, -80.21) * mm});
            skLineSegment(sketch, "E117.right", {"start": v(1258.43, 65.4) * mm, "end": v(1258.43, -80.21) * mm});
            skSolve(sketch);
        }
        {
            var Q0;
            Q0 = qSketchRegion(id + "F76", true);
            extrude(context, id + "F77", {"entities" : qUnion([Q0]), "operationType" : NewBodyOperationType.REMOVE, "oppositeDirection" : true, "depth" : 307 * mm, "offsetDistance" : 25 * mm});
        }
    });
